# Revit family: NEON FRAME 29W_LKB9634WW_CW
name_source: partatom
category: Luminarias
units: mm (PartAtom-declared; Revit-internal decimal feet)

## family parameters
Compartido = No
Corte con vacíos al cargar = No
Cota de conector redondo = Diámetro de uso
Origen de luz = Sí
Punto de cálculo de habitación = No
Se basa en plano de trabajo = Sí
Siempre vertical = No
Tipo de pieza = Normal

## types (2) — shared parameters
Cambio de temperatura de color de luz atenuada = <Ninguno>
Fabricante = BRILLANT
Filtro de color = 16777215
Longitud de línea de emisión = 200 mm  [stored 0.656168 ft]
Lámpara = NICHIA
Watt per fixture = 29
zero-valued in all types: Elevación por defecto

## per-type parameters (varying)
| type | Archivo de red fotométrica | Comentarios de vataje | Descripción | Modelo | Ángulo de inclinación |
| EMP_LKB9634WW.120 | LKB9634WW.IES | 90-277V | LUMINARIA LINEAL CON DIFUSOR PARA EMPOTRAR CON 96 LED TIPO NICHIA CON UNA POTENCIA DE 29W, CUERPO DE ALUMINIO EXTRUIDO CUBIERTO CON POLVO GRIS OSCURO CON CUBIERTA DE ACERO INOXIDABLE Y VIDRIO TEMPLADO DE 6MM, HOUSING DE ALUMINIO, CON UNA DIMENSION DE 80MM DE PROFUNDO POR 1007 DE LARGO EN LA LUMINARIA, CUENTA CON 545 LUMENES A UNA TEMPERATURA EN BLANCO CALIDO DE 3000K, CORRIENTE DE OPERACIÓN A 212mA, ON/OFF, DIMEABLE (OPCIONAL) EN TRIAC, CABLE H05RN L0.5M, IRC 80, IK07, IP67, ANGULO DE APERTURA A 120 GRADOS EN STOCK, ALIMENTADA A 90-277V. | LKB9634WW.120 | 120.00° |
| EMP_LKB9634CW.120 | generic | 100-277V | LUMINARIA LINEAL CON DIFUSOR PARA EMPOTRAR CON 96 LED TIPO NICHIA CON UNA POTENCIA DE 29W, CUERPO DE ALUMINIO EXTRUIDO CUBIERTO CON POLVO GRIS OSCURO CON CUBIERTA DE ACERO INOXIDABLE Y VIDRIO TEMPLADO DE 6MM, HOUSING DE ALUMINIO, CON UNA DIMENSION DE 80MM DE PROFUNDO POR 1007 DE LARGO EN LA LUMINARIA, CUENTA CON 602 LUMENES A UNA TEMPERATURA EN BLANCO FRIO DE 6000K, CORRIENTE DE OPERACIÓN A 212mA, ON/OFF, DIMEABLE (OPCIONAL) EN TRIAC, CABLE H05RN L0.5M, IRC 80, IK07, IP67, ANGULO DE APERTURA A 120 GRADOS EN STOCK, ALIMENTADA A 100-277V. | LKB9634CW.120 | 30.00° |

note: [stored X ft] marks values corroborated as IEEE doubles in the binary element streams (Revit-internal decimal feet)

## geometry (parser evidence)
native form markers: Blend x2
no freeform markers — native parametric forms only
